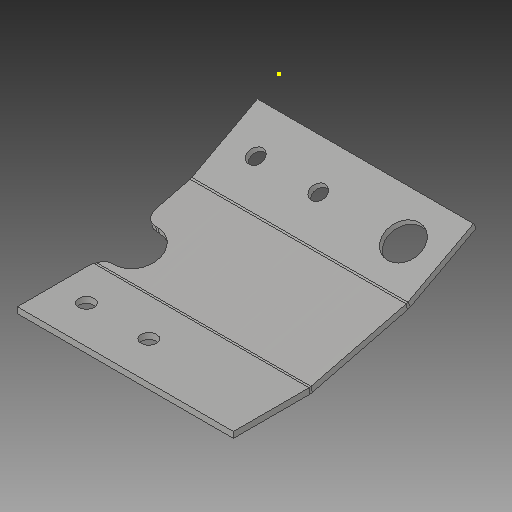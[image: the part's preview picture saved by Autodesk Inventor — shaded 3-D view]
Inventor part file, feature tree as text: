
AUTODESK INVENTOR PART (.ipt)
format: ipt  version: 2018 (Build 220112000, 112)  size: 270,848 bytes
history: native  units: mm
features: other x8, sketch x7, sheet_metal_op x3, hole x3, reference x2, plane x1, fillet x1, projected_geometry x1
ambient origin geometry x8: Origin, YZ Plane, XZ Plane, XY Plane, X Axis, Y Axis, Z Axis, Center Point
bodies: Body1 (feature_tree)
feature tree (26):
  other  "model.ipt"
  plane  "Work Plane1"
  sketch  "Sketch2"  dims[d7=10.0mm d9=5.0mm]
  sheet_metal_op  "Contour Flange1"
  hole  "Hole1"  [1 undecoded]
  hole  "Hole7"  [1 undecoded]
  hole  "Hole8"  [1 undecoded]
  sketch  "Sketch11"  dims[d17=20.0mm]
  fillet  "Fillet1"  Radius=180.0mm
  other  "Plate3"
  sheet_metal_op  "Bend2"
  sheet_metal_op  "Corner1"
  sketch  "Sketch7"  dims[d10=5.0mm d11=2.5mm]
  sketch  "Sketch8"  dims[d12=10.0mm d13=6.25mm d14=180.0mm]
  sketch  "Sketch9"  dims[d15=6.25mm]
  sketch  "Sketch10"  dims[d16=5.0mm]
  reference  "Reference1"
  reference  "Reference2"
  sketch  "Sketch12"  dims[d18=5.0mm d19=6.25mm d20=39.0mm d21=39.0mm d22=13.0mm d23=6.0mm d24=4.0mm d25=2.0mm d26=90.0deg d27=5.0mm d28=20.594885mm d74=62.052154mm d75=31.026077mm d76=26.0mm d77=52.0mm d78=81.718239mm d79=40.85912mm d80=26.0mm d81=52.0mm d82=13.0mm d83=6.0mm d84=4.0mm d85=2.0mm d86=90.0deg d87=5.0mm d88=20.594885mm d89=63.10912mm d90=31.55456mm d91=26.0mm d92=52.0mm d93=13.0mm d94=6.0mm d95=4.0mm d96=2.0mm d97=90.0deg d98=5.0mm d99=20.594885mm d100=20.0mm d101=20.0mm d102=302.737mm d103=30.0mm d104=302.737mm d105=5.0mm d106=0.0mm d107=18.5mm d108=30.0mm d109=62.052154mm d110=31.026077mm d111=31.026077mm d112=5.0mm d113=0.0mm d114=10.0mm d29=1.0mm d30=1.0mm]
  projected_geometry  "Projected Loop1"
  other  "Cut1"
  other  "Cut2"
  parser-record x1  (decoder bookkeeping rows leaked as tree rows — omitted from the tree; the rows remain in map.json)
  other  "modul.iam"
  other  "vange:1"
  other  "Definition1"
note: 3 required parameter values undecoded (feature->parameter linkage not recoverable at this tier; creation-order binding heuristic only, values carry confidence <= 0.55)
note: 1 file-system path scrubbed to <path> (originals preserved in map.json)
